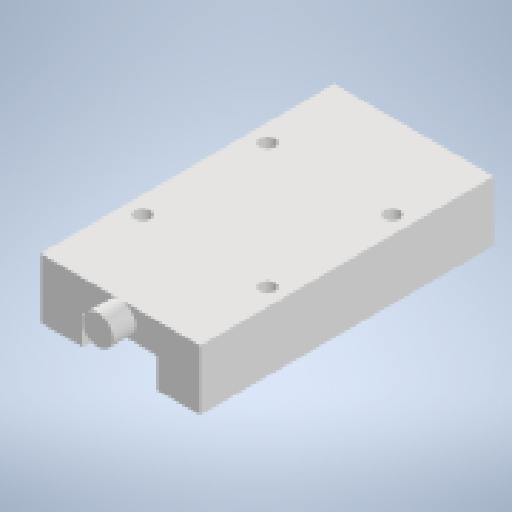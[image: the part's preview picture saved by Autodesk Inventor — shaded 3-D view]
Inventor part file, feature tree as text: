
AUTODESK INVENTOR PART (.ipt)
format: ipt  version: 2023 (Build 270158000, 158)  size: 153,600 bytes
history: native  units: mm
features: extrude x3, sketch x3
ambient origin geometry x8: Origin, YZ Plane, XZ Plane, XY Plane, X Axis, Y Axis, Z Axis, Center Point
bodies: Solid1 (feature_tree)
feature tree (6):
  extrude  "Extrusion1"  Depth=12.0mm
  extrude  "Extrusion2"  Depth=6.0mm
  extrude  "Extrusion3"  Depth=3.0mm
  sketch  "Sketch1"  dims[d0=32.0mm d1=12.0mm]
  sketch  "Sketch2"  dims[d2=8.5mm d3=6.0mm]
  sketch  "Sketch3"  dims[d4=58.8mm d5=0.0mm d6=3.0mm d7=25.0mm d8=25.0mm d9=4.0mm d10=0.0mm d11=6.0mm d12=4.5mm d13=0.0mm]
